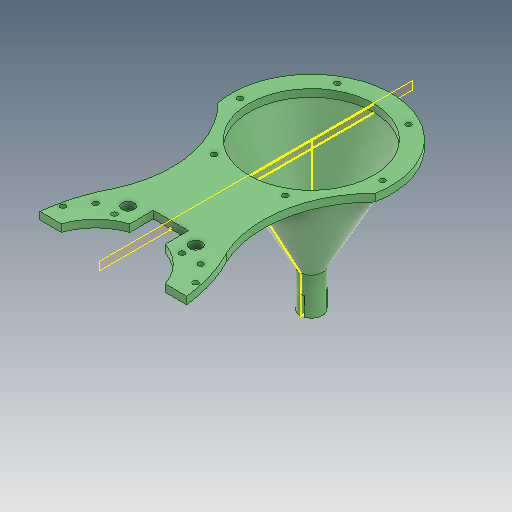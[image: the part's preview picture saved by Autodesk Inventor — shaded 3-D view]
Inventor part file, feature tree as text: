
AUTODESK INVENTOR PART (.ipt)
format: ipt  version: 2020.3 (Build 243373000, 373)  size: 225,792 bytes
history: native  units: mm
features: other x3, sketch x2, plane x1
ambient origin geometry x8: Origin, YZ Plane, XZ Plane, XY Plane, X Axis, Y Axis, Z Axis, Center Point
bodies: Solid1 (feature_tree)
feature tree (6):
  other  "OneLensHolder.ipt"
  other  "Solid1::OneLensHolder.ipt"
  other  "TaggingFeature1"
  sketch  "Sketch1"  dims[d0=10.0mm]
  sketch  "Sketch3"
  plane  "Work Plane1"
